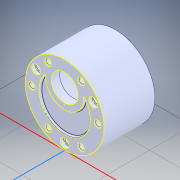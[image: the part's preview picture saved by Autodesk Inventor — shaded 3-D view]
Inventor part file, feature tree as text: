
AUTODESK INVENTOR PART (.ipt)
format: ipt  version: 2022 (Build 260153000, 153)  size: 219,648 bytes
history: native  units: mm
features: other x3, sketch x1, projected_geometry x1, fillet x1
ambient origin geometry x8: Origin, YZ Plane, XZ Plane, XY Plane, X Axis, Y Axis, Z Axis, Center Point
bodies: Body1 (feature_tree)
feature tree (6):
  other  "Твердое тело1"
  other  "Непосредственное редактирование1"
  sketch  "Эскиз1"
  projected_geometry  "Спроецированная петля1"
  fillet  "Fillet1"  [1 undecoded]
  other  "Перенос1"
note: 1 required parameter value undecoded (feature->parameter linkage not recoverable at this tier; creation-order binding heuristic only, values carry confidence <= 0.55)
